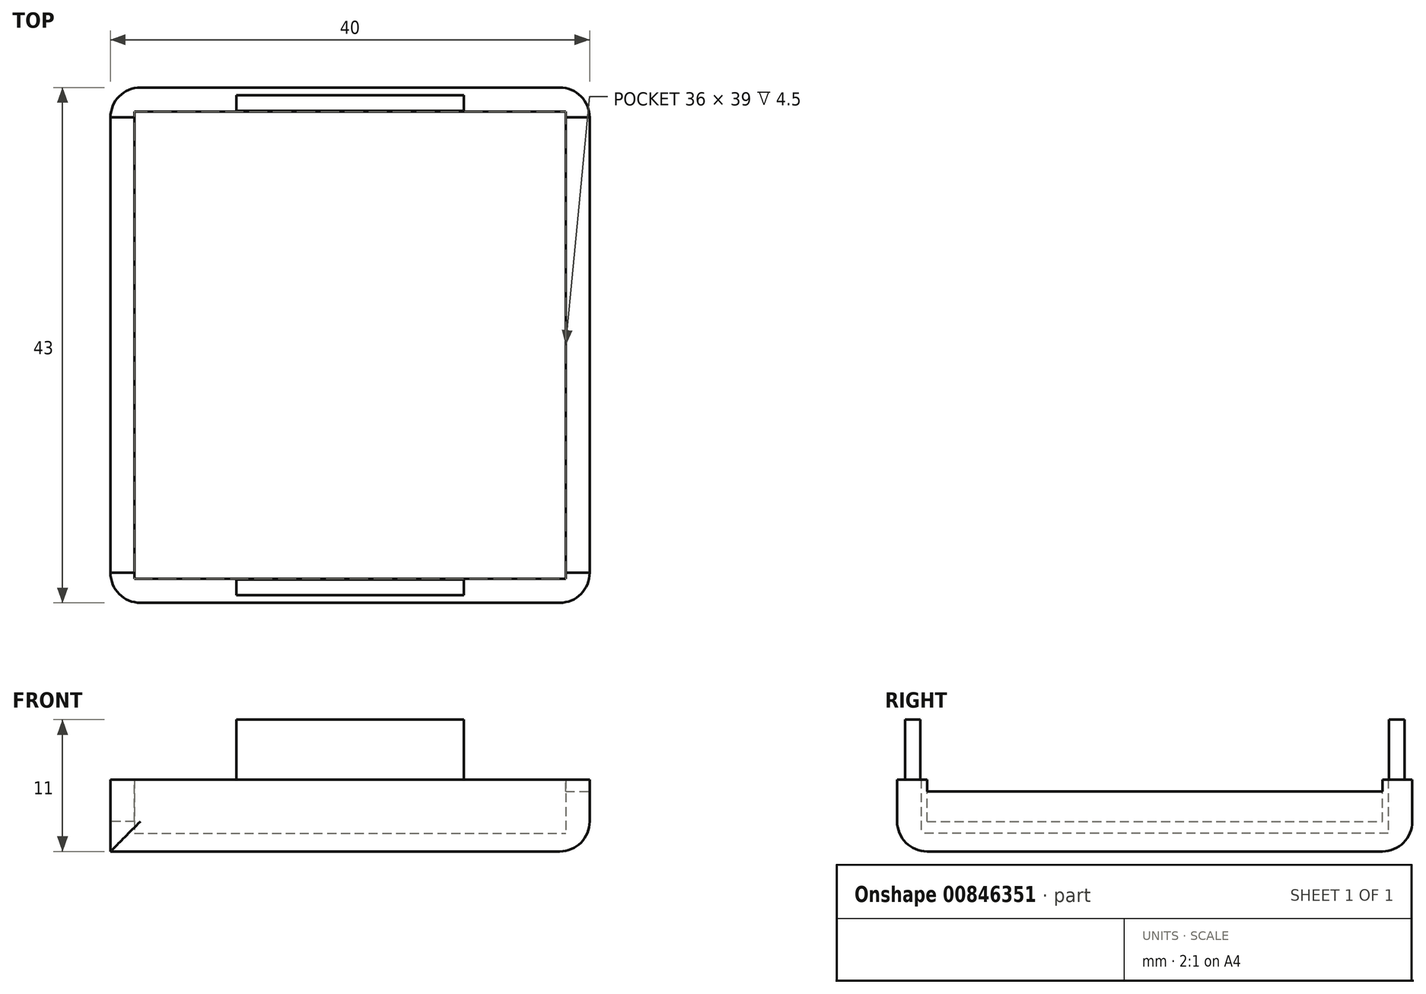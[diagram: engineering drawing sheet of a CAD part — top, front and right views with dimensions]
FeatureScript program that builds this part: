
annotation { "Feature Type Name" : "Feature", "Feature Type Description" : "" }
export const myFeature = defineFeature(function(context is Context, id is Id, definition is map)
    precondition{}
    {
        {
            var Q0;
            Q0=qCreatedBy(makeId("Top.planeOp"),FACE);
            var sketch = newSketch(context, id + "F0", { "sketchPlane" : qUnion([Q0])});
            skLineSegment(sketch, "E0.bottom", {"start": v(18, -19.5) * mm, "end": v(-18, -19.5) * mm});
            skLineSegment(sketch, "E0.top", {"start": v(18, 19.5) * mm, "end": v(-18, 19.5) * mm});
            skLineSegment(sketch, "E0.left", {"start": v(18, -19.5) * mm, "end": v(18, 19.5) * mm});
            skLineSegment(sketch, "E0.right", {"start": v(-18, -19.5) * mm, "end": v(-18, 19.5) * mm});
            skPoint(sketch, "E0.middle", {"position": v(0, 0) * mm});
            skLineSegment(sketch, "E1.bottom", {"start": v(20, -21.5) * mm, "end": v(-20, -21.5) * mm});
            skLineSegment(sketch, "E1.top", {"start": v(20, 21.5) * mm, "end": v(-20, 21.5) * mm});
            skLineSegment(sketch, "E1.left", {"start": v(20, -21.5) * mm, "end": v(20, 21.5) * mm});
            skLineSegment(sketch, "E1.right", {"start": v(-20, -21.5) * mm, "end": v(-20, 21.5) * mm});
            skSolve(sketch);
        }
        {
            var Q0;
            Q0=makeQuery(id+"F0.imprint","IMPRINT",FACE,{"disambiguationData":[TD([[makeQuery(id+"F0.imprint","IMPRINT",EDGE,{"derivedFrom":sQuery(id+"F0.wireOp",EDGE,"E0.bottom")}),-1.0]])]});
            var Q1;
            Q1=makeQuery(id+"F0.imprint","IMPRINT",FACE,{"disambiguationData":[TD([[makeQuery(id+"F0.imprint","IMPRINT",EDGE,{"derivedFrom":sQuery(id+"F0.wireOp",EDGE,"E0.bottom")}),1.0]])]});
            extrude(context, id + "F1", {"entities" : qUnion([Q0, Q1]), "depth" : 1.5 * mm, "offsetDistance" : 25 * mm});
        }
        {
            var Q0;
            Q0=makeQuery(id+"F0.imprint","IMPRINT",FACE,{"disambiguationData":[TD([[makeQuery(id+"F0.imprint","IMPRINT",EDGE,{"derivedFrom":sQuery(id+"F0.wireOp",EDGE,"E0.bottom")}),1.0]])]});
            extrude(context, id + "F2", {"entities" : qUnion([Q0]), "operationType" : NewBodyOperationType.ADD, "depth" : 6 * mm, "offsetDistance" : 25 * mm});
        }
        {
            var Q0;
            Q0=makeQuery(id+"F2.opExtrude","CAP_FACE",FACE,{"disambiguationData":[OSD([sQuery(id+"F0.wireOp",EDGE,"E0.bottom"),sQuery(id+"F0.wireOp",EDGE,"E0.top"),sQuery(id+"F0.wireOp",EDGE,"E0.left"),sQuery(id+"F0.wireOp",EDGE,"E0.right"),sQuery(id+"F0.wireOp",EDGE,"E1.bottom"),sQuery(id+"F0.wireOp",EDGE,"E1.top"),sQuery(id+"F0.wireOp",EDGE,"E1.left"),sQuery(id+"F0.wireOp",EDGE,"E1.right")])],"isStart":false});
            var sketch = newSketch(context, id + "F3", { "sketchPlane" : qUnion([Q0])});
            skLineSegment(sketch, "E2.bottom", {"start": v(-16.56, -19) * mm, "end": v(-21.56, -19) * mm});
            skLineSegment(sketch, "E2.top", {"start": v(-16.56, 19) * mm, "end": v(-21.56, 19) * mm});
            skLineSegment(sketch, "E2.left", {"start": v(-16.56, -19) * mm, "end": v(-16.56, 19) * mm});
            skLineSegment(sketch, "E2.right", {"start": v(-21.56, -19) * mm, "end": v(-21.56, 19) * mm});
            skPoint(sketch, "E2.middle", {"position": v(-19.06, 0) * mm});
            skPoint(sketch, "E2.middle.positionSnap0", {"position": v(-20, 0) * mm});
            skPoint(sketch, "E2.centerSnap0", {"position": v(-20, 0) * mm});
            skPoint(sketch, "E3.MirrorP", {"position": v(20, 0) * mm});
            skLineSegment(sketch, "E4.MirrorCS", {"start": v(16.56, -19) * mm, "end": v(16.56, 19) * mm});
            skPoint(sketch, "E5.MirrorP", {"position": v(19.06, 0) * mm});
            skLineSegment(sketch, "E6.MirrorCS", {"start": v(21.56, -19) * mm, "end": v(21.56, 19) * mm});
            skLineSegment(sketch, "E7.MirrorCS", {"start": v(16.56, 19) * mm, "end": v(21.56, 19) * mm});
            skLineSegment(sketch, "E8.MirrorCS", {"start": v(16.56, -19) * mm, "end": v(21.56, -19) * mm});
            skSolve(sketch);
        }
        {
            var Q0;
            {var subQ0=sQuery(id+"F3.wireOp",EDGE,"E2.bottom");var subQ1=makeQuery(id+"F2.opExtrude","CAP_EDGE",EDGE,{"disambiguationData":[OSD([sQuery(id+"F0.wireOp",EDGE,"E1.right")])],"isStart":false});var subQ2=makeQuery(id+"F3.imprint","INTERSECT",VERTEX,{"derivedFrom":[subQ1,subQ0]});Q0=makeQuery(id+"F3.imprint","IMPRINT",FACE,{"disambiguationData":[TD([[makeQuery(id+"F3.imprint","IMPRINT",EDGE,{"disambiguationData":[TD([[subQ2,1.0]])],"derivedFrom":subQ0}),-1.0]])]});}
            extrude(context, id + "F4", {"entities" : qUnion([Q0]), "operationType" : NewBodyOperationType.REMOVE, "oppositeDirection" : true, "depth" : 3.5 * mm, "offsetDistance" : 25 * mm});
        }
        {
            var Q0;
            {var subQ0=sQuery(id+"F0.wireOp",EDGE,"E1.right");var subQ1=sQuery(id+"F0.wireOp",EDGE,"E1.bottom");Q0=makeQuery(id+"F2.boolean.opBoolean","MERGE",EDGE,{"derivedFrom":[makeQuery(id+"F1.opExtrude","SWEPT_EDGE",EDGE,{"disambiguationData":[OSD([subQ1,subQ0])]}),makeQuery(id+"F2.opExtrude","SWEPT_EDGE",EDGE,{"disambiguationData":[OSD([subQ1,subQ0])]})]});}
            var Q1;
            {var subQ0=sQuery(id+"F0.wireOp",EDGE,"E1.left");var subQ1=sQuery(id+"F0.wireOp",EDGE,"E1.bottom");Q1=makeQuery(id+"F2.boolean.opBoolean","MERGE",EDGE,{"derivedFrom":[makeQuery(id+"F1.opExtrude","SWEPT_EDGE",EDGE,{"disambiguationData":[OSD([subQ1,subQ0])]}),makeQuery(id+"F2.opExtrude","SWEPT_EDGE",EDGE,{"disambiguationData":[OSD([subQ1,subQ0])]})]});}
            var Q2;
            {var subQ0=sQuery(id+"F0.wireOp",EDGE,"E1.left");var subQ1=sQuery(id+"F0.wireOp",EDGE,"E1.top");Q2=makeQuery(id+"F2.boolean.opBoolean","MERGE",EDGE,{"derivedFrom":[makeQuery(id+"F1.opExtrude","SWEPT_EDGE",EDGE,{"disambiguationData":[OSD([subQ1,subQ0])]}),makeQuery(id+"F2.opExtrude","SWEPT_EDGE",EDGE,{"disambiguationData":[OSD([subQ1,subQ0])]})]});}
            var Q3;
            {var subQ0=sQuery(id+"F0.wireOp",EDGE,"E1.right");var subQ1=sQuery(id+"F0.wireOp",EDGE,"E1.top");Q3=makeQuery(id+"F2.boolean.opBoolean","MERGE",EDGE,{"derivedFrom":[makeQuery(id+"F1.opExtrude","SWEPT_EDGE",EDGE,{"disambiguationData":[OSD([subQ1,subQ0])]}),makeQuery(id+"F2.opExtrude","SWEPT_EDGE",EDGE,{"disambiguationData":[OSD([subQ1,subQ0])]})]});}
            var Q4;
            Q4=makeQuery(id+"F1.opExtrude","CAP_EDGE",EDGE,{"disambiguationData":[OSD([sQuery(id+"F0.wireOp",EDGE,"E1.bottom")])],"isStart":true});
            var Q5;
            Q5=makeQuery(id+"F1.opExtrude","CAP_EDGE",EDGE,{"disambiguationData":[OSD([sQuery(id+"F0.wireOp",EDGE,"E1.left")])],"isStart":true});
            var Q6;
            Q6=makeQuery(id+"F1.opExtrude","CAP_EDGE",EDGE,{"disambiguationData":[OSD([sQuery(id+"F0.wireOp",EDGE,"E1.top")])],"isStart":true});
            fillet(context, id + "F5", {"entities" : qUnion([Q0, Q1, Q2, Q3, Q4, Q5, Q6]), "radius" : 2.5 * mm, "tangentPropagation" : true, "allowEdgeOverflow" : false});
        }
        {
            var Q0;
            Q0=makeQuery(id+"F2.opExtrude","CAP_FACE",FACE,{"disambiguationData":[OSD([sQuery(id+"F0.wireOp",EDGE,"E0.bottom"),sQuery(id+"F0.wireOp",EDGE,"E0.top"),sQuery(id+"F0.wireOp",EDGE,"E0.left"),sQuery(id+"F0.wireOp",EDGE,"E0.right"),sQuery(id+"F0.wireOp",EDGE,"E1.bottom"),sQuery(id+"F0.wireOp",EDGE,"E1.top"),sQuery(id+"F0.wireOp",EDGE,"E1.left"),sQuery(id+"F0.wireOp",EDGE,"E1.right")])],"isStart":false});
            var sketch = newSketch(context, id + "F6", { "sketchPlane" : qUnion([Q0])});
            skLineSegment(sketch, "E9.bottom", {"start": v(9.5, 19.55) * mm, "end": v(-9.5, 19.55) * mm});
            skLineSegment(sketch, "E9.top", {"start": v(9.5, 20.85) * mm, "end": v(-9.5, 20.85) * mm});
            skLineSegment(sketch, "E9.left", {"start": v(9.5, 19.55) * mm, "end": v(9.5, 20.85) * mm});
            skLineSegment(sketch, "E9.right", {"start": v(-9.5, 19.55) * mm, "end": v(-9.5, 20.85) * mm});
            skPoint(sketch, "E9.middle", {"position": v(0, 20.2) * mm});
            skLineSegment(sketch, "E10.MirrorCS", {"start": v(-9.5, -19.55) * mm, "end": v(-9.5, -20.85) * mm});
            skLineSegment(sketch, "E11.MirrorCS", {"start": v(9.5, -19.55) * mm, "end": v(9.5, -20.85) * mm});
            skLineSegment(sketch, "E12.MirrorCS", {"start": v(9.5, -20.85) * mm, "end": v(-9.5, -20.85) * mm});
            skLineSegment(sketch, "E13.MirrorCS", {"start": v(9.5, -19.55) * mm, "end": v(-9.5, -19.55) * mm});
            skPoint(sketch, "E14.MirrorP", {"position": v(0, -20.2) * mm});
            skSolve(sketch);
        }
        {
            var Q0;
            Q0=makeQuery(id+"F6.imprint","IMPRINT",FACE,{"disambiguationData":[TD([[makeQuery(id+"F6.imprint","IMPRINT",EDGE,{"derivedFrom":sQuery(id+"F6.wireOp",EDGE,"E9.bottom")}),-1.0]])]});
            var Q1;
            Q1=makeQuery(id+"F6.imprint","IMPRINT",FACE,{"disambiguationData":[TD([[makeQuery(id+"F6.imprint","IMPRINT",EDGE,{"derivedFrom":sQuery(id+"F6.wireOp",EDGE,"E10.MirrorCS")}),1.0]])]});
            extrude(context, id + "F7", {"entities" : qUnion([Q0, Q1]), "operationType" : NewBodyOperationType.ADD, "depth" : 5 * mm, "offsetDistance" : 25 * mm});
        }
        {
            var Q0;
            {var subQ0=sQuery(id+"F3.wireOp",EDGE,"E7.MirrorCS");var subQ1=makeQuery(id+"F2.opExtrude","CAP_EDGE",EDGE,{"disambiguationData":[OSD([sQuery(id+"F0.wireOp",EDGE,"E1.left")])],"isStart":false});var subQ2=makeQuery(id+"F3.imprint","INTERSECT",VERTEX,{"derivedFrom":[subQ1,subQ0]});Q0=makeQuery(id+"F3.imprint","IMPRINT",FACE,{"disambiguationData":[TD([[makeQuery(id+"F3.imprint","IMPRINT",EDGE,{"disambiguationData":[TD([[subQ2,1.0]])],"derivedFrom":subQ0}),-1.0]])]});}
            extrude(context, id + "F8", {"entities" : qUnion([Q0]), "operationType" : NewBodyOperationType.REMOVE, "oppositeDirection" : true, "depth" : 1 * mm, "offsetDistance" : 25 * mm});
        }
    });
